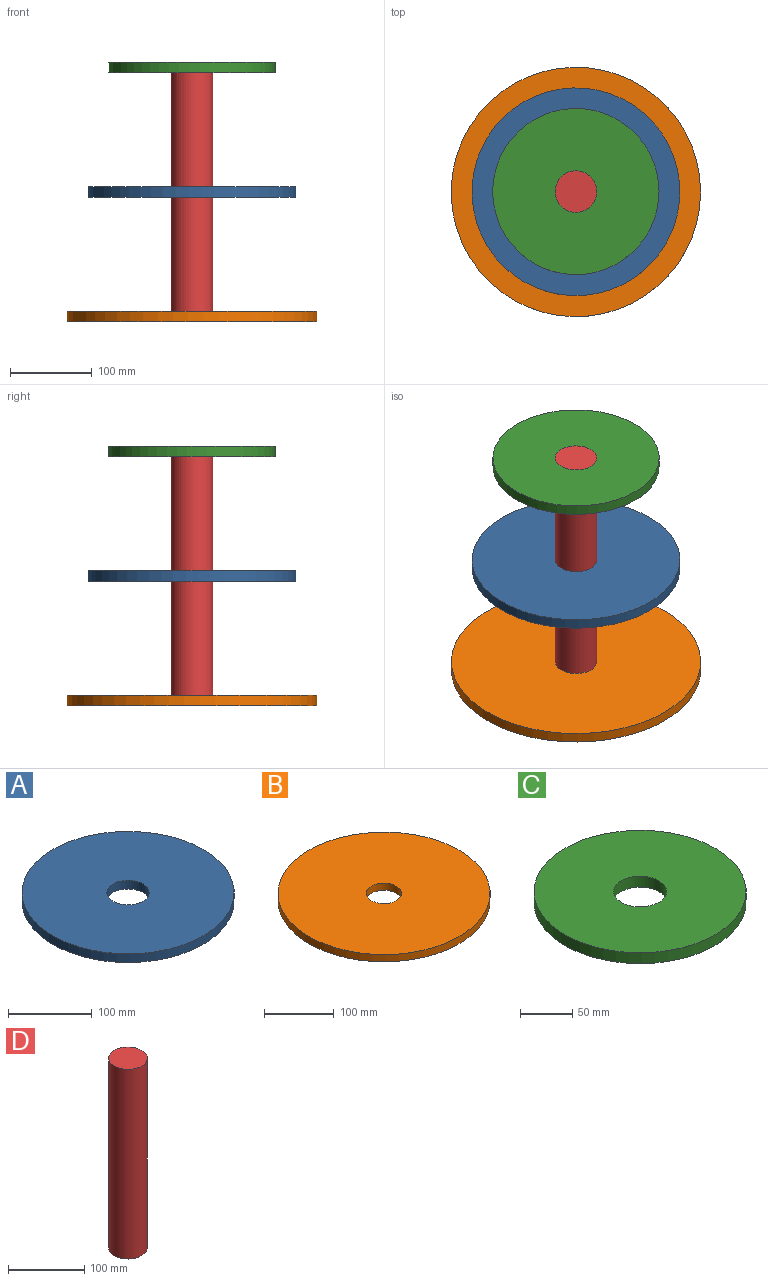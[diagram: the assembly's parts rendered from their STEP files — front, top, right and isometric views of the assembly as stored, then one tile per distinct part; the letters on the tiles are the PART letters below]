
ASSEMBLY  parts=4 mates=3
PART A: 4 faces, bbox 254x254x12.7 mm
  f0: cylinder r=127mm len=254mm, axis (0,0,-1), area 10134.1mm2, adj f1,f2
  f1: plane 254x254mm, normal (0,0,1), area 48643.9mm2, adj f0,f3
  f2: plane 254x254mm, normal (0,0,-1), area 48643.9mm2, adj f0,f3
  f3: cylinder r=25.4mm len=50.8mm, axis (0,0,1), area 2026.8mm2, adj f1,f2
PART B: 4 faces, bbox 304.8x304.8x12.7 mm
  f0: cylinder r=152.4mm len=304.8mm, axis (0,0,-1), area 12161mm2, adj f1,f2
  f1: plane 304.8x304.8mm, normal (0,0,1), area 70939mm2, adj f0,f3
  f2: plane 304.8x304.8mm, normal (0,0,-1), area 70939mm2, adj f0,f3
  f3: cylinder r=25.4mm len=50.8mm, axis (0,0,1), area 2026.8mm2, adj f1,f2
PART C: 4 faces, bbox 203.2x203.2x12.7 mm
  f0: cylinder r=101.6mm len=203.2mm, axis (0,0,-1), area 8107.3mm2, adj f1,f2
  f1: plane 203.2x203.2mm, normal (0,0,1), area 30402.4mm2, adj f0,f3
  f2: plane 203.2x203.2mm, normal (0,0,-1), area 30402.4mm2, adj f0,f3
  f3: cylinder r=25.4mm len=50.8mm, axis (0,0,1), area 2026.8mm2, adj f1,f2
PART D: 3 faces, bbox 50.8x50.8x304.8 mm
  f0: cylinder r=25.4mm len=304.8mm, axis (0,0,-1), area 48643.9mm2, adj f1,f2
  f1: plane 50.8x50.8mm, normal (0,0,1), area 2026.8mm2, adj f0
  f2: plane 50.8x50.8mm, normal (0,0,-1), area 2026.8mm2, adj f0
PLACE A t=(-345.52,-298.2,10.29)mm
PLACE B t=(-345.52,-298.2,-142.11)mm
PLACE C t=(-345.52,-298.2,162.69)mm
PLACE D t=(-345.52,-298.2,-129.41)mm
MATE fastened C.f0 <-> D.f0  axis (0,0,1) through (-345.52,-298.2,175.39)mm
MATE fastened A.f0 <-> D.f0  axis (0,0,1) through (-345.52,-298.2,22.99)mm
MATE fastened B.f0 <-> D.f0  axis (0,0,1) through (-345.52,-298.2,-129.41)mm
